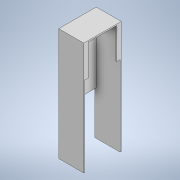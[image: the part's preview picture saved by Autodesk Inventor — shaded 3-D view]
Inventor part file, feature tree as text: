
AUTODESK INVENTOR PART (.ipt)
format: ipt  version: 2020 (Build 240168000, 168)  size: 132,608 bytes
history: native  units: mm
features: extrude x4, sketch x4, mirror x1
ambient origin geometry x8: Origin, YZ Plane, XZ Plane, XY Plane, X Axis, Y Axis, Z Axis, Center Point
bodies: Solid1 (feature_tree)
feature tree (9):
  extrude  "Extrusion1"  Depth=60.0mm
  extrude  "Extrusion2"  Depth=38.0mm
  extrude  "Extrusion3"  Depth=2.0mm TaperAngle=0.0deg
  mirror  "Mirror1"
  extrude  "Extrusion4"  Depth=50.0mm
  sketch  "Sketch1"  dims[d0=40.0mm d1=60.0mm]
  sketch  "Sketch2"  dims[d2=2.0mm d3=38.0mm]
  sketch  "Sketch3"  dims[d4=180.0mm d5=0.0mm d6=2.0mm d7=0.0mm]
  sketch  "Sketch4"  dims[d8=2.0mm d9=50.0mm d10=5.0mm d11=0.0mm d12=70.0mm d13=5.0mm d14=0.0mm]
